# Revit family: SABRINA_1104LM_3000K_BLANC
name_source: partatom
category: Lighting Fixtures
units: mm (PartAtom-declared; Revit-internal decimal feet)

## family parameters
Always vertical = Yes
Cut with Voids When Loaded = No
Host = Wall
Light Source = Yes
OmniClass Number = 23.80.70.00
OmniClass Title = Lighting
Part Type = Normal
Room Calculation Point = No
Round Connector Dimension = Use Diameter
Shared = No

## types (1)
- SABRINA_1104LM_3000K_BLANC
    Alimentation Driver = AC 220-240V / 50Hz
    Color Filter = 16777215
    Default Elevation = 0 mm  [stored 0 ft]
    Diffuseur = Verre opale trempé
    Dimensions = 300 x 58 x 72 mm
    Dimming Lamp Color Temperature Shift = <None>
    Durée de vie = 50 000 heures
    Emit from Line Length = 610 mm
    Fintion = Blanc
    IRC = >80
    Light Source Symbol Size = 610 mm
    Maintien du flux = L80B10 (50 000 heures)
    Matériau = Corps en fonte d’aluminium
    Puissance nominale = 2x8W
    Type = Applique avec interrupteur ON/OFF
    Type de lampe = LED SMD 2835

note: [stored X ft] marks values corroborated as IEEE doubles in the binary element streams (Revit-internal decimal feet)

## geometry (parser evidence)
native form markers: Sweep x2
no freeform markers — native parametric forms only
